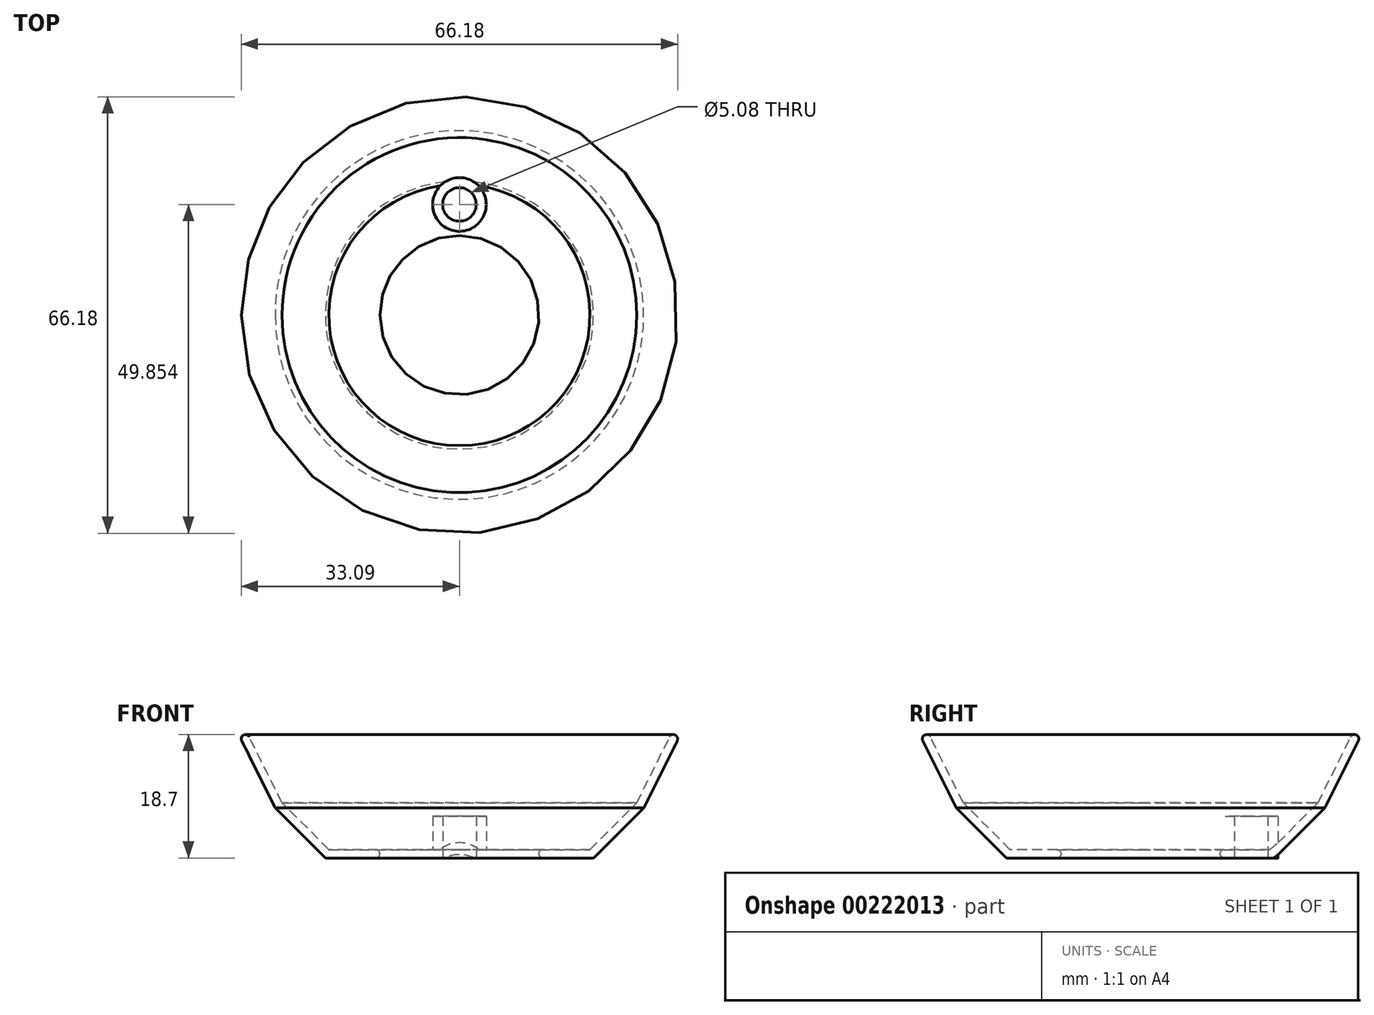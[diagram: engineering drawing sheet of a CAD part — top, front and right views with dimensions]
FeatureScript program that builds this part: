
annotation { "Feature Type Name" : "Feature", "Feature Type Description" : "" }
export const myFeature = defineFeature(function(context is Context, id is Id, definition is map)
    precondition{}
    {
        {
            var Q0;
            Q0=qCreatedBy(makeId("Front.planeOp"),FACE);
            var sketch = newSketch(context, id + "F0", { "sketchPlane" : qUnion([Q0])});
            skLineSegment(sketch, "E0", {"start": v(12.7, 0) * mm, "end": v(20.32, 0) * mm});
            skLineSegment(sketch, "E1", {"start": v(20.32, 0) * mm, "end": v(27.94, 7.62) * mm});
            skLineSegment(sketch, "E2", {"start": v(27.94, 7.62) * mm, "end": v(33.02, 17.78) * mm});
            skLineSegment(sketch, "E3", {"start": v(33.02, 17.78) * mm, "end": v(32.45, 18.06) * mm});
            skLineSegment(sketch, "E4", {"start": v(12.7, 1.27) * mm, "end": v(19.8, 1.27) * mm});
            skLineSegment(sketch, "E5", {"start": v(31.88, 18.35) * mm, "end": v(26.9, 8.37) * mm});
            skLineSegment(sketch, "E6", {"start": v(19.8, 1.27) * mm, "end": v(26.9, 8.37) * mm});
            skArc(sketch, "E7", {"start": v(12.7, 1.27) * mm, "mid": v(12.07, 0.64) * mm, "end": v(12.7, 0) * mm});
            skArc(sketch, "E8", {"start": v(33.02, 17.78) * mm, "mid": v(32.74, 18.63) * mm, "end": v(31.88, 18.35) * mm});
            skLineSegment(sketch, "E9", {"start": v(0, 0) * mm, "end": v(0, 4.45) * mm, "construction": true});
            skSolve(sketch);
        }
        {
            var Q0;
            Q0 = qSketchRegion(id + "F0", true);
            var Q1;
            Q1=sQuery(id+"F0.wireOp",EDGE,"E9");
            revolve(context, id + "F1", {"entities" : qUnion([Q0]), "axis" : qUnion([Q1]), "revolveType" : RevolveType.FULL});
        }
        {
            var Q0;
            Q0=qCreatedBy(makeId("Top.planeOp"),FACE);
            var sketch = newSketch(context, id + "F2", { "sketchPlane" : qUnion([Q0])});
            skCircle(sketch, "E10", {"center": v(0, 16.76) * mm, "radius": 4.06 * mm});
            skCircle(sketch, "E11", {"center": v(0, 16.76) * mm, "radius": 2.54 * mm});
            skSolve(sketch);
        }
        {
            var Q0;
            Q0 = qSketchRegion(id + "F2", true);
            extrude(context, id + "F3", {"entities" : qUnion([Q0]), "operationType" : NewBodyOperationType.ADD, "depth" : 6.35 * mm});
        }
        {
            var Q0;
            Q0=qCreatedBy(makeId("Top.planeOp"),FACE);
            var sketch = newSketch(context, id + "F4", { "sketchPlane" : qUnion([Q0])});
            skCircle(sketch, "E12", {"center": v(0, 16.76) * mm, "radius": 2.54 * mm});
            skSolve(sketch);
        }
        {
            var Q0;
            Q0 = qSketchRegion(id + "F4", true);
            extrude(context, id + "F5", {"entities" : qUnion([Q0]), "operationType" : NewBodyOperationType.REMOVE, "oppositeDirection" : true, "depth" : 6.35 * mm, "hasSecondDirection" : true, "secondDirectionOppositeDirection" : false, "secondDirectionDepth" : 25.4 * mm});
        }
    });
